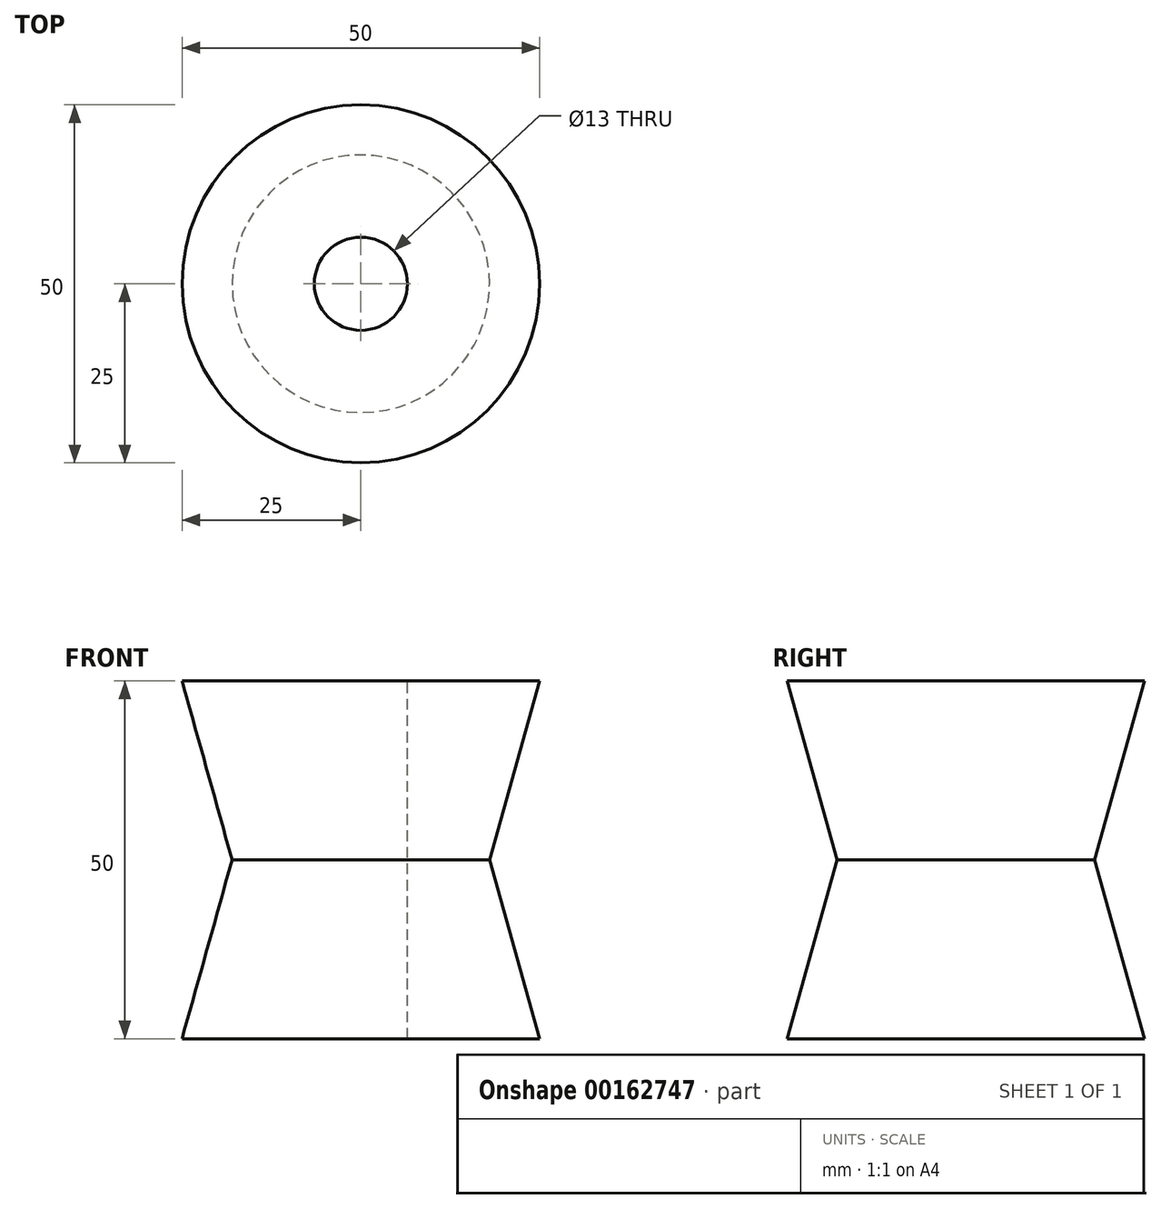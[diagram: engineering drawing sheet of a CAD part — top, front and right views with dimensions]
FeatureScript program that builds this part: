
annotation { "Feature Type Name" : "Feature", "Feature Type Description" : "" }
export const myFeature = defineFeature(function(context is Context, id is Id, definition is map)
    precondition{}
    {
        {
            var Q0;
            Q0=qCreatedBy(makeId("Right.planeOp"),FACE);
            var sketch = newSketch(context, id + "F0", { "sketchPlane" : qUnion([Q0])});
            skLineSegment(sketch, "E0", {"start": v(0, 50) * mm, "end": v(-25, 50) * mm});
            skLineSegment(sketch, "E1", {"start": v(-25, 0) * mm, "end": v(0, 0) * mm});
            skLineSegment(sketch, "E2", {"start": v(0, 0) * mm, "end": v(0, 50) * mm});
            skLineSegment(sketch, "E3", {"start": v(0, 25) * mm, "end": v(-18, 25) * mm, "construction": true});
            skPoint(sketch, "E3.endSnap0", {"position": v(0, 25) * mm});
            skLineSegment(sketch, "E4", {"start": v(-25, 50) * mm, "end": v(-18, 25) * mm});
            skLineSegment(sketch, "E5", {"start": v(-25, 0) * mm, "end": v(-18, 25) * mm});
            skSolve(sketch);
        }
        {
            var Q0;
            Q0=makeQuery(id+"F0.imprint","IMPRINT",FACE,{"disambiguationData":[TD([[makeQuery(id+"F0.imprint","IMPRINT",EDGE,{"derivedFrom":sQuery(id+"F0.wireOp",EDGE,"E0")}),1.0]])]});
            var Q1;
            Q1=sQuery(id+"F0.wireOp",EDGE,"E2");
            revolve(context, id + "F1", {"entities" : qUnion([Q0]), "axis" : qUnion([Q1]), "revolveType" : RevolveType.FULL});
        }
        {
            var Q0;
            Q0=makeQuery(id+"F1.opRevolve","SWEPT_FACE",FACE,{"disambiguationData":[OSD([sQuery(id+"F0.wireOp",EDGE,"E0")])]});
            var sketch = newSketch(context, id + "F2", { "sketchPlane" : qUnion([Q0])});
            skCircle(sketch, "E6", {"center": v(0, 0) * mm, "radius": 6.5 * mm});
            skSolve(sketch);
        }
        {
            var Q0;
            Q0=makeQuery(id+"F2.imprint","IMPRINT",FACE,{"disambiguationData":[TD([[makeQuery(id+"F2.imprint","IMPRINT",EDGE,{"derivedFrom":sQuery(id+"F2.wireOp",EDGE,"E6")}),1.0]])]});
            extrude(context, id + "F3", {"entities" : qUnion([Q0]), "operationType" : NewBodyOperationType.REMOVE, "endBound" : BoundingType.THROUGH_ALL, "oppositeDirection" : true, "depth" : 25 * mm});
        }
    });
